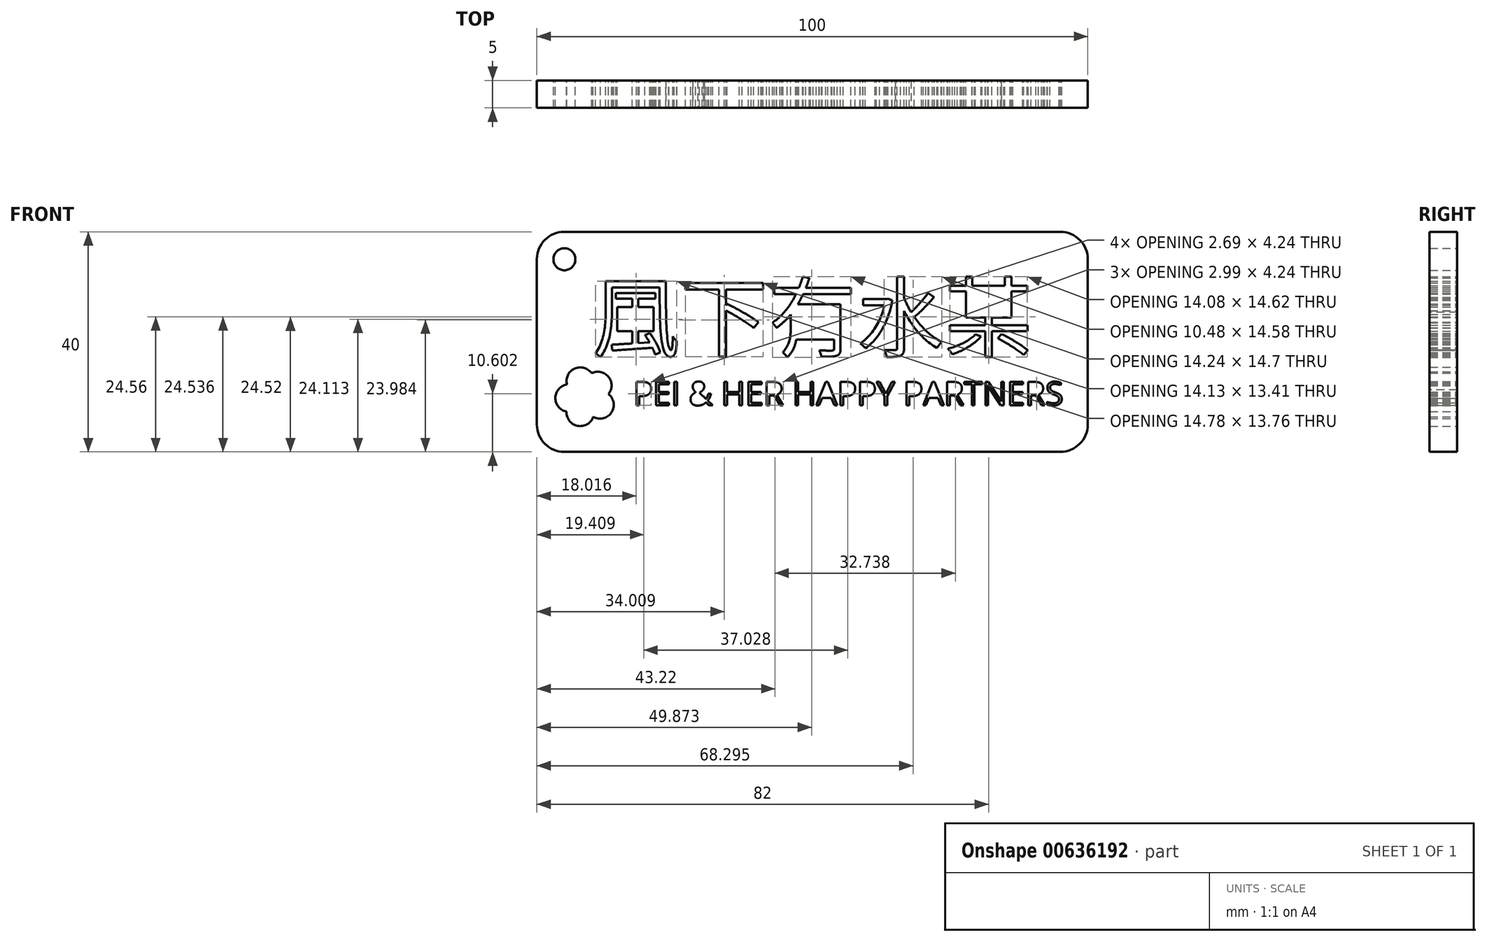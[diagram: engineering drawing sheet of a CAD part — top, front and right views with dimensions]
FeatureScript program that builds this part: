
annotation { "Feature Type Name" : "Feature", "Feature Type Description" : "" }
export const myFeature = defineFeature(function(context is Context, id is Id, definition is map)
    precondition{}
    {
        {
            var Q0;
            Q0=qCreatedBy(makeId("Front.planeOp"),FACE);
            var sketch = newSketch(context, id + "F0", { "sketchPlane" : qUnion([Q0])});
            skPoint(sketch, "E0", {"position": v(0, 0) * mm});
            skPoint(sketch, "E1", {"position": v(-50, 0) * mm});
            skLineSegment(sketch, "E2.top", {"start": v(-45, 20) * mm, "end": v(112.41, 20) * mm});
            skLineSegment(sketch, "E2.left", {"start": v(-50, 0) * mm, "end": v(-50, 15) * mm});
            skPoint(sketch, "E3.visualSharp", {"position": v(-50, 20) * mm});
            skArc(sketch, "E3.filletArc", {"start": v(-45, 20) * mm, "mid": v(-48.54, 18.54) * mm, "end": v(-50, 15) * mm});
            skPoint(sketch, "E4.visualSharp", {"position": v(-33.84, 20) * mm});
            skCircle(sketch, "E5", {"center": v(-45, 15) * mm, "radius": 2 * mm});
            skPoint(sketch, "E6.MirrorP", {"position": v(50, 0) * mm});
            skLineSegment(sketch, "E7.MirrorCS", {"start": v(50, 0) * mm, "end": v(50, 15) * mm});
            skPoint(sketch, "E8.MirrorP", {"position": v(50, 20) * mm});
            skPoint(sketch, "E9.MirrorP", {"position": v(33.84, 20) * mm});
            skLineSegment(sketch, "E10.MirrorCS", {"start": v(45, 20) * mm, "end": v(-112.41, 20) * mm});
            skArc(sketch, "E11.MirrorCS", {"start": v(45, 20) * mm, "mid": v(48.54, 18.54) * mm, "end": v(50, 15) * mm});
            skPoint(sketch, "E12.MirrorP", {"position": v(50, -20) * mm});
            skPoint(sketch, "E13.MirrorP", {"position": v(-50, -20) * mm});
            skArc(sketch, "E14.MirrorCS", {"start": v(-50, -15) * mm, "mid": v(-48.54, -18.54) * mm, "end": v(-45, -20) * mm});
            skArc(sketch, "E15.MirrorCS", {"start": v(50, -15) * mm, "mid": v(48.54, -18.54) * mm, "end": v(45, -20) * mm});
            skLineSegment(sketch, "E16.MirrorCS", {"start": v(-45, -20) * mm, "end": v(45, -20) * mm});
            skArc(sketch, "E17.MirrorCS", {"start": v(-45, -20) * mm, "mid": v(-48.54, -18.54) * mm, "end": v(-50, -15) * mm});
            skArc(sketch, "E18.MirrorCS", {"start": v(45, -20) * mm, "mid": v(48.54, -18.54) * mm, "end": v(50, -15) * mm});
            skLineSegment(sketch, "E19.MirrorCS", {"start": v(-50, 0) * mm, "end": v(-50, -15) * mm});
            skLineSegment(sketch, "E20.MirrorCS", {"start": v(50, 0) * mm, "end": v(50, -15) * mm});
            skText(sketch, "E21", { "text": "風下有水某", "fontName": "NotoSansCJKtc-Regular.otf"});
            skText(sketch, "E22", { "text": "PEI & HER HAPPY PARTNERS", "fontName": "OpenSans-Regular.ttf"});
            skCircle(sketch, "E23", {"center": v(-41.15, -9.97) * mm, "radius": 3 * mm});
            skCircle(sketch, "E24", {"center": v(-42.12, -7.13) * mm, "radius": 2.5 * mm});
            skCircle(sketch, "E25", {"center": v(-44.14, -10.21) * mm, "radius": 2.5 * mm});
            skCircle(sketch, "E26", {"center": v(-42.12, -12.8) * mm, "radius": 2.5 * mm});
            skCircle(sketch, "E27", {"center": v(-38.54, -11.46) * mm, "radius": 2.5 * mm});
            skCircle(sketch, "E28", {"center": v(-38.94, -7.93) * mm, "radius": 2.5 * mm});
            const initialGuessF0  = {"E21": [-0.04, -0.00152, 1, 0, 0.01152], "E22": [-0.03252, -0.01152, 1, 0, 0.00428]};
            skSetInitialGuess(sketch, initialGuessF0);
            skSolve(sketch);
        }
        {
            var Q0;
            Q0 = qSketchRegion(id + "F0", true);
            extrude(context, id + "F1", {"entities" : qUnion([Q0]), "depth" : 5 * mm, "offsetDistance" : 25 * mm});
        }
    });
